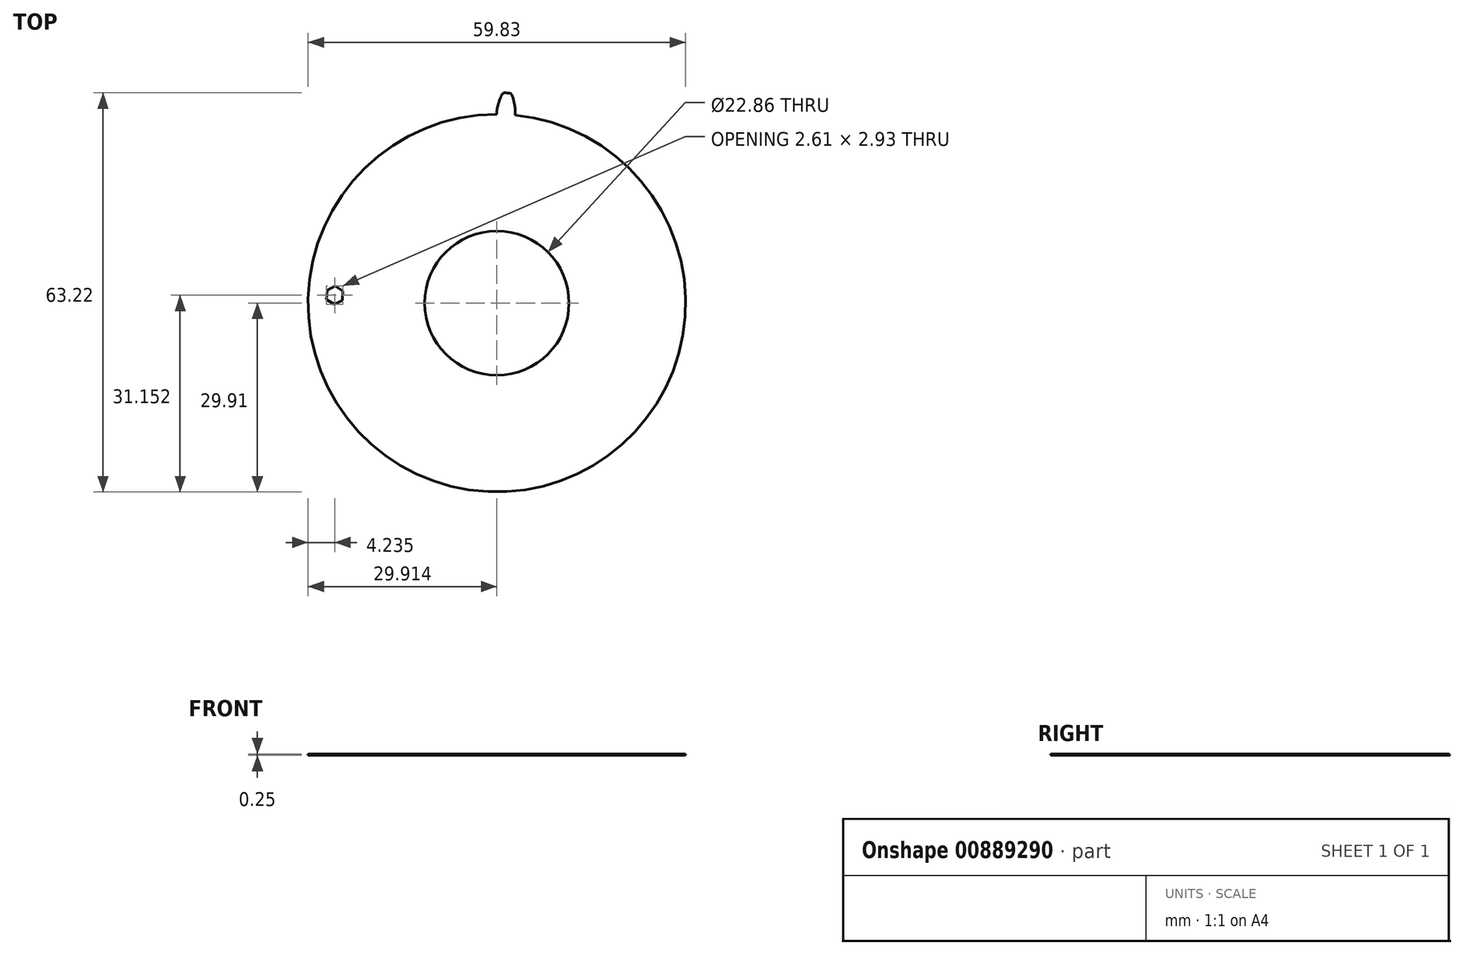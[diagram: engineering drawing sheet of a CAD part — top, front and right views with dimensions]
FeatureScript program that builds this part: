
annotation { "Feature Type Name" : "Feature", "Feature Type Description" : "" }
export const myFeature = defineFeature(function(context is Context, id is Id, definition is map)
    precondition{}
    {
        {
            assignVariable(context, id + "F0", {"name" : "N", "anyValue" : 16 * 2.5});
        }
        {
            assignVariable(context, id + "F1", {"name" : "Swid", "anyValue" : 0.25});
        }
        {
            var Q0;
            Q0=qCreatedBy(makeId("Top.planeOp"),FACE);
            var sketch = newSketch(context, id + "F2", { "sketchPlane" : qUnion([Q0])});
            skCircle(sketch, "E0", {"center": v(0, 0) * mm, "radius": 30.36 * mm, "construction": true});
            skCircle(sketch, "E1", {"center": v(0, 0) * mm, "radius": 31.75 * mm, "construction": true});
            skCircle(sketch, "E2", {"center": v(0, 0) * mm, "radius": 33.34 * mm});
            skLineSegment(sketch, "E3", {"start": v(0, 0) * mm, "end": v(0, 30.36) * mm, "construction": true});
            skLineSegment(sketch, "E4", {"start": v(0, 0) * mm, "end": v(1.99, 30.3) * mm, "construction": true});
            skLineSegment(sketch, "E5", {"start": v(0, 0) * mm, "end": v(3.96, 30.1) * mm, "construction": true});
            skLineSegment(sketch, "E6", {"start": v(0, 0) * mm, "end": v(5.92, 29.78) * mm, "construction": true});
            skLineSegment(sketch, "E7", {"start": v(0, 0) * mm, "end": v(7.86, 29.33) * mm, "construction": true});
            skCircle(sketch, "E8", {"center": v(0, 0) * mm, "radius": 29.91 * mm});
            skLineSegment(sketch, "E9", {"start": v(1.99, 30.3) * mm, "end": v(0, 30.43) * mm, "construction": true});
            skLineSegment(sketch, "E10", {"start": v(3.96, 30.1) * mm, "end": v(0.02, 30.62) * mm, "construction": true});
            skLineSegment(sketch, "E11", {"start": v(5.92, 29.78) * mm, "end": v(0.08, 30.94) * mm, "construction": true});
            skLineSegment(sketch, "E12", {"start": v(7.86, 29.33) * mm, "end": v(0.18, 31.39) * mm, "construction": true});
            skLineSegment(sketch, "E13", {"start": v(0, 0) * mm, "end": v(9.76, 28.75) * mm, "construction": true});
            skLineSegment(sketch, "E14", {"start": v(9.76, 28.75) * mm, "end": v(0.35, 31.95) * mm, "construction": true});
            skLineSegment(sketch, "E15", {"start": v(0, 0) * mm, "end": v(11.62, 28.05) * mm, "construction": true});
            skLineSegment(sketch, "E16", {"start": v(0, 0) * mm, "end": v(13.43, 27.23) * mm, "construction": true});
            skLineSegment(sketch, "E17", {"start": v(0, 0) * mm, "end": v(15.18, 26.3) * mm, "construction": true});
            skLineSegment(sketch, "E18", {"start": v(11.62, 28.05) * mm, "end": v(0.6, 32.61) * mm, "construction": true});
            skLineSegment(sketch, "E19", {"start": v(13.43, 27.23) * mm, "end": v(0.95, 33.38) * mm, "construction": true});
            skLineSegment(sketch, "E20", {"start": v(15.18, 26.3) * mm, "end": v(1.41, 34.24) * mm, "construction": true});
            skLineSegment(sketch, "E21", {"start": v(0, 0) * mm, "end": v(16.87, 25.25) * mm, "construction": true});
            skLineSegment(sketch, "E22", {"start": v(0, 0) * mm, "end": v(18.48, 24.09) * mm, "construction": true});
            skLineSegment(sketch, "E23", {"start": v(0, 0) * mm, "end": v(20.02, 22.83) * mm, "construction": true});
            skLineSegment(sketch, "E24", {"start": v(0, 0) * mm, "end": v(21.47, 21.47) * mm, "construction": true});
            skLineSegment(sketch, "E25", {"start": v(0, 0) * mm, "end": v(22.83, 20.02) * mm, "construction": true});
            skLineSegment(sketch, "E26", {"start": v(16.87, 25.25) * mm, "end": v(2, 35.18) * mm, "construction": true});
            skLineSegment(sketch, "E27", {"start": v(18.48, 24.09) * mm, "end": v(2.72, 36.19) * mm, "construction": true});
            skLineSegment(sketch, "E28", {"start": v(20.02, 22.83) * mm, "end": v(3.58, 37.24) * mm, "construction": true});
            skLineSegment(sketch, "E29", {"start": v(21.47, 21.47) * mm, "end": v(4.6, 38.33) * mm, "construction": true});
            skLineSegment(sketch, "E30", {"start": v(22.83, 20.02) * mm, "end": v(5.8, 39.44) * mm, "construction": true});
            skLineSegment(sketch, "E31", {"start": v(0, 0) * mm, "end": v(24.09, 18.48) * mm, "construction": true});
            skLineSegment(sketch, "E32", {"start": v(24.09, 18.48) * mm, "end": v(7.15, 40.56) * mm, "construction": true});
            skLineSegment(sketch, "E33", {"start": v(0, 0) * mm, "end": v(25.25, 16.87) * mm, "construction": true});
            skLineSegment(sketch, "E34", {"start": v(25.25, 16.87) * mm, "end": v(8.68, 41.65) * mm, "construction": true});
            skSolve(sketch);
        }
        {
            var Q0;
            Q0=qCreatedBy(makeId("Top.planeOp"),FACE);
            var sketch = newSketch(context, id + "F3", { "sketchPlane" : qUnion([Q0])});
            skLineSegment(sketch, "E35.0", {"start": v(24.09, 18.48) * mm, "end": v(7.15, 40.56) * mm, "construction": true});
            skLineSegment(sketch, "E35.1", {"start": v(22.83, 20.02) * mm, "end": v(5.8, 39.44) * mm, "construction": true});
            skLineSegment(sketch, "E35.2", {"start": v(21.47, 21.47) * mm, "end": v(4.6, 38.33) * mm, "construction": true});
            skLineSegment(sketch, "E35.3", {"start": v(20.02, 22.83) * mm, "end": v(3.58, 37.24) * mm, "construction": true});
            skLineSegment(sketch, "E35.4", {"start": v(18.48, 24.09) * mm, "end": v(2.72, 36.19) * mm, "construction": true});
            skLineSegment(sketch, "E35.5", {"start": v(16.87, 25.25) * mm, "end": v(2, 35.18) * mm, "construction": true});
            skLineSegment(sketch, "E35.6", {"start": v(15.18, 26.3) * mm, "end": v(1.41, 34.24) * mm, "construction": true});
            skLineSegment(sketch, "E35.7", {"start": v(13.43, 27.23) * mm, "end": v(0.95, 33.38) * mm, "construction": true});
            skLineSegment(sketch, "E35.8", {"start": v(11.62, 28.05) * mm, "end": v(0.6, 32.61) * mm, "construction": true});
            skLineSegment(sketch, "E35.9", {"start": v(9.76, 28.75) * mm, "end": v(0.35, 31.95) * mm, "construction": true});
            skLineSegment(sketch, "E35.10", {"start": v(7.86, 29.33) * mm, "end": v(0.18, 31.39) * mm, "construction": true});
            skLineSegment(sketch, "E35.11", {"start": v(5.92, 29.78) * mm, "end": v(0.08, 30.94) * mm, "construction": true});
            skLineSegment(sketch, "E35.12", {"start": v(3.96, 30.1) * mm, "end": v(0.02, 30.62) * mm, "construction": true});
            skLineSegment(sketch, "E35.13", {"start": v(1.99, 30.3) * mm, "end": v(0, 30.43) * mm, "construction": true});
            skCircle(sketch, "E35.14", {"center": v(0, 0) * mm, "radius": 30.36 * mm});
            skCircle(sketch, "E35.15", {"center": v(0, 0) * mm, "radius": 29.91 * mm});
            skCircle(sketch, "E35.16", {"center": v(0, 0) * mm, "radius": 31.75 * mm, "construction": true});
            skCircle(sketch, "E35.17", {"center": v(0, 0) * mm, "radius": 33.34 * mm});
            skLineSegment(sketch, "E36.0", {"start": v(25.25, 16.87) * mm, "end": v(8.68, 41.65) * mm, "construction": true});
            skLineSegment(sketch, "E37.0", {"start": v(0, 0) * mm, "end": v(0, 30.36) * mm, "construction": true});
            skFitSpline(sketch, "E38", {"points": [v(0, 30.36) * mm, v(0, 30.43) * mm, v(0.02, 30.62) * mm, v(0.08, 30.94) * mm, v(0.18, 31.39) * mm, v(0.35, 31.95) * mm, v(0.6, 32.61) * mm, v(0.95, 33.38) * mm, v(1.41, 34.24) * mm, v(2, 35.18) * mm, v(2.72, 36.19) * mm, v(3.58, 37.24) * mm, v(4.6, 38.33) * mm, v(5.8, 39.44) * mm, v(7.15, 40.56) * mm, v(8.68, 41.65) * mm, v(0, 0) * mm], "startDerivative": vector(0.68, 15.67) * mm, "endDerivative": vector(-81.92, -392.9) * mm});
            skLineSegment(sketch, "E39", {"start": v(0.29, 31.75) * mm, "end": v(0, 0) * mm, "construction": true});
            skLineSegment(sketch, "E40", {"start": v(0, 0) * mm, "end": v(1.6, 33.3) * mm, "construction": true});
            skFitSpline(sketch, "E41.MirrorCS", {"points": [v(2.93, 30.22) * mm, v(2.93, 30.29) * mm, v(2.93, 30.48) * mm, v(2.9, 30.8) * mm, v(2.85, 31.26) * mm, v(2.73, 31.83) * mm, v(2.54, 32.52) * mm, v(2.27, 33.32) * mm, v(1.9, 34.22) * mm, v(1.4, 35.21) * mm, v(0.78, 36.28) * mm, v(0.02, 37.41) * mm, v(-0.89, 38.6) * mm, v(-1.96, 39.82) * mm, v(-3.2, 41.06) * mm, v(-4.63, 42.3) * mm, v(0, 0) * mm], "startDerivative": vector(0.83, 15.67) * mm, "endDerivative": vector(43.65, -398.97) * mm});
            skLineSegment(sketch, "E42", {"start": v(2.93, 30.22) * mm, "end": v(2.88, 29.77) * mm});
            skLineSegment(sketch, "E43", {"start": v(0, 30.36) * mm, "end": v(0, 29.91) * mm});
            skSolve(sketch);
        }
        {
            var Q0;
            {var subQ3=sQuery(id+"F3.wireOp",EDGE,"E41.MirrorCS");var subQ6=sQuery(id+"F3.wireOp",EDGE,"E35.17");var subQ8=makeQuery(id+"F3.imprint","INTERSECT",VERTEX,{"disambiguationData":[OD(1.0)],"derivedFrom":[subQ6,subQ3]});Q0=makeQuery(id+"F3.imprint","IMPRINT",FACE,{"disambiguationData":[TD([[makeQuery(id+"F3.imprint","IMPRINT",EDGE,{"disambiguationData":[TD([[subQ8,-1.0]])],"derivedFrom":subQ6}),1.0]])]});}
            var Q1;
            {var subQ3=sQuery(id+"F3.wireOp",EDGE,"E41.MirrorCS");var subQ5=sQuery(id+"F3.wireOp",EDGE,"E35.15");var subQ6=makeQuery(id+"F3.imprint","INTERSECT",VERTEX,{"derivedFrom":[subQ5,subQ3]});Q1=makeQuery(id+"F3.imprint","IMPRINT",FACE,{"disambiguationData":[TD([[makeQuery(id+"F3.imprint","IMPRINT",EDGE,{"disambiguationData":[TD([[subQ6,-1.0]])],"derivedFrom":subQ5}),1.0]])]});}
            var Q2;
            {var subQ2=sQuery(id+"F3.wireOp",EDGE,"E42");Q2=makeQuery(id+"F3.imprint","IMPRINT",FACE,{"disambiguationData":[TD([[makeQuery(id+"F3.imprint","IMPRINT",EDGE,{"derivedFrom":subQ2}),-1.0]])]});}
            extrude(context, id + "F4", {"entities" : qUnion([Q0, Q1, Q2]), "depth" : (getVariable(context, 'Swid')) * mm, "offsetDistance" : 25.4 * mm});
        }
        {
            var Q0;
            Q0=qCreatedBy(makeId("Right.planeOp"),FACE);
            var sketch = newSketch(context, id + "F5", { "sketchPlane" : qUnion([Q0])});
            skLineSegment(sketch, "E44", {"start": v(0, 0) * mm, "end": v(0, 43.3) * mm, "construction": true});
            skSolve(sketch);
        }
        {
            var Q0;
            Q0=makeQuery(id+"F4.opExtrude","SWEPT_EDGE",EDGE,{"disambiguationData":[OSD([sQuery(id+"F3.wireOp",EDGE,"E35.17"),sQuery(id+"F3.wireOp",EDGE,"E41.MirrorCS")])]});
            var Q1;
            Q1=makeQuery(id+"F4.opExtrude","SWEPT_EDGE",EDGE,{"disambiguationData":[OSD([sQuery(id+"F3.wireOp",EDGE,"E35.17"),sQuery(id+"F3.wireOp",EDGE,"E38")])]});
            fillet(context, id + "F6", {"entities" : qUnion([Q0, Q1]), "radius" : 0.5 * mm, "tangentPropagation" : true, "allowEdgeOverflow" : false});
        }
        {
            var Q0;
            Q0=makeQuery(id+"F4.opExtrude","SWEPT_BODY",BODY,{"disambiguationData":[OSD([sQuery(id+"F3.wireOp",EDGE,"E35.15"),sQuery(id+"F3.wireOp",EDGE,"E35.17"),sQuery(id+"F3.wireOp",EDGE,"E38"),sQuery(id+"F3.wireOp",EDGE,"E41.MirrorCS"),sQuery(id+"F3.wireOp",EDGE,"9305e2c8-a00a-4cbc-a3b2-8fc88bc1717c"),sQuery(id+"F3.wireOp",EDGE,"f762f43d-eaf9-45ff-b6cd-062fd530227c")])]});
            var Q1;
            Q1=sQuery(id+"F5.wireOp",EDGE,"E44");
            circularPattern(context, id + "F7", {"operationType" : NewBodyOperationType.ADD, "entities" : qUnion([Q0]), "axis" : qUnion([Q1]), "angle" : (360 / getVariable(context, 'N')) * degree, "instanceCount" : getVariable(context, 'N'), "oppositeDirection" : true});
        }
        {
            var Q0;
            Q0=makeQuery(id+"F4.opExtrude","SWEPT_BODY",BODY,{"disambiguationData":[OSD([sQuery(id+"F3.wireOp",EDGE,"E35.15"),sQuery(id+"F3.wireOp",EDGE,"E35.17"),sQuery(id+"F3.wireOp",EDGE,"E38"),sQuery(id+"F3.wireOp",EDGE,"E41.MirrorCS"),sQuery(id+"F3.wireOp",EDGE,"E42"),sQuery(id+"F3.wireOp",EDGE,"E43")])]});
            transform(context, id + "F8", {"entities" : qUnion([Q0]), "transformType" : TransformType.TRANSLATION_3D, "dx" : 100.58 * mm, "dy" : 0 * mm, "dz" : 0 * mm, "makeCopy" : true});
        }
        {
            var Q0;
            {var subQ0=makeQuery(id+"F4.opExtrude","CAP_FACE",FACE,{"disambiguationData":[OSD([sQuery(id+"F3.wireOp",EDGE,"E35.15"),sQuery(id+"F3.wireOp",EDGE,"E35.17"),sQuery(id+"F3.wireOp",EDGE,"E38"),sQuery(id+"F3.wireOp",EDGE,"E41.MirrorCS"),sQuery(id+"F3.wireOp",EDGE,"E42"),sQuery(id+"F3.wireOp",EDGE,"E43")])],"isStart":false});Q0=makeQuery(id+"F7.boolean.opBoolean","MERGE",FACE,{"derivedFrom":[subQ0,makeQuery(id+"F7.opPattern","COPY",FACE,{"derivedFrom":subQ0,"instanceName":"1"}),makeQuery(id+"F7.opPattern","COPY",FACE,{"derivedFrom":subQ0,"instanceName":"2"}),makeQuery(id+"F7.opPattern","COPY",FACE,{"derivedFrom":subQ0,"instanceName":"3"}),makeQuery(id+"F7.opPattern","COPY",FACE,{"derivedFrom":subQ0,"instanceName":"4"}),makeQuery(id+"F7.opPattern","COPY",FACE,{"derivedFrom":subQ0,"instanceName":"5"}),makeQuery(id+"F7.opPattern","COPY",FACE,{"derivedFrom":subQ0,"instanceName":"6"}),makeQuery(id+"F7.opPattern","COPY",FACE,{"derivedFrom":subQ0,"instanceName":"7"}),makeQuery(id+"F7.opPattern","COPY",FACE,{"derivedFrom":subQ0,"instanceName":"8"}),makeQuery(id+"F7.opPattern","COPY",FACE,{"derivedFrom":subQ0,"instanceName":"9"}),makeQuery(id+"F7.opPattern","COPY",FACE,{"derivedFrom":subQ0,"instanceName":"10"}),makeQuery(id+"F7.opPattern","COPY",FACE,{"derivedFrom":subQ0,"instanceName":"11"}),makeQuery(id+"F7.opPattern","COPY",FACE,{"derivedFrom":subQ0,"instanceName":"12"}),makeQuery(id+"F7.opPattern","COPY",FACE,{"derivedFrom":subQ0,"instanceName":"13"}),makeQuery(id+"F7.opPattern","COPY",FACE,{"derivedFrom":subQ0,"instanceName":"14"}),makeQuery(id+"F7.opPattern","COPY",FACE,{"derivedFrom":subQ0,"instanceName":"15"}),makeQuery(id+"F7.opPattern","COPY",FACE,{"derivedFrom":subQ0,"instanceName":"16"}),makeQuery(id+"F7.opPattern","COPY",FACE,{"derivedFrom":subQ0,"instanceName":"17"}),makeQuery(id+"F7.opPattern","COPY",FACE,{"derivedFrom":subQ0,"instanceName":"18"}),makeQuery(id+"F7.opPattern","COPY",FACE,{"derivedFrom":subQ0,"instanceName":"19"}),makeQuery(id+"F7.opPattern","COPY",FACE,{"derivedFrom":subQ0,"instanceName":"20"}),makeQuery(id+"F7.opPattern","COPY",FACE,{"derivedFrom":subQ0,"instanceName":"21"}),makeQuery(id+"F7.opPattern","COPY",FACE,{"derivedFrom":subQ0,"instanceName":"22"}),makeQuery(id+"F7.opPattern","COPY",FACE,{"derivedFrom":subQ0,"instanceName":"23"}),makeQuery(id+"F7.opPattern","COPY",FACE,{"derivedFrom":subQ0,"instanceName":"24"}),makeQuery(id+"F7.opPattern","COPY",FACE,{"derivedFrom":subQ0,"instanceName":"25"}),makeQuery(id+"F7.opPattern","COPY",FACE,{"derivedFrom":subQ0,"instanceName":"26"}),makeQuery(id+"F7.opPattern","COPY",FACE,{"derivedFrom":subQ0,"instanceName":"27"}),makeQuery(id+"F7.opPattern","COPY",FACE,{"derivedFrom":subQ0,"instanceName":"28"}),makeQuery(id+"F7.opPattern","COPY",FACE,{"derivedFrom":subQ0,"instanceName":"29"}),makeQuery(id+"F7.opPattern","COPY",FACE,{"derivedFrom":subQ0,"instanceName":"30"}),makeQuery(id+"F7.opPattern","COPY",FACE,{"derivedFrom":subQ0,"instanceName":"31"}),makeQuery(id+"F7.opPattern","COPY",FACE,{"derivedFrom":subQ0,"instanceName":"32"}),makeQuery(id+"F7.opPattern","COPY",FACE,{"derivedFrom":subQ0,"instanceName":"33"}),makeQuery(id+"F7.opPattern","COPY",FACE,{"derivedFrom":subQ0,"instanceName":"34"}),makeQuery(id+"F7.opPattern","COPY",FACE,{"derivedFrom":subQ0,"instanceName":"35"}),makeQuery(id+"F7.opPattern","COPY",FACE,{"derivedFrom":subQ0,"instanceName":"36"}),makeQuery(id+"F7.opPattern","COPY",FACE,{"derivedFrom":subQ0,"instanceName":"37"}),makeQuery(id+"F7.opPattern","COPY",FACE,{"derivedFrom":subQ0,"instanceName":"38"}),makeQuery(id+"F7.opPattern","COPY",FACE,{"derivedFrom":subQ0,"instanceName":"39"})]});}
            var sketch = newSketch(context, id + "F9", { "sketchPlane" : qUnion([Q0])});
            skCircle(sketch, "E45", {"center": v(0, 0) * mm, "radius": 4.1 * mm});
            skLineSegment(sketch, "E46", {"start": v(29.9, 0.9) * mm, "end": v(0, 0) * mm, "construction": true});
            skLineSegment(sketch, "E47", {"start": v(2.62, -3.15) * mm, "end": v(2.43, 3.3) * mm});
            skSolve(sketch);
        }
        {
            var Q0;
            {var subQ0=sQuery(id+"F9.wireOp",EDGE,"E47");Q0=makeQuery(id+"F9.imprint","IMPRINT",FACE,{"disambiguationData":[TD([[makeQuery(id+"F9.imprint","IMPRINT",EDGE,{"derivedFrom":subQ0}),1.0]])]});}
            extrude(context, id + "F10", {"entities" : qUnion([Q0]), "operationType" : NewBodyOperationType.REMOVE, "endBound" : BoundingType.THROUGH_ALL, "oppositeDirection" : true, "depth" : 25.4 * mm, "offsetDistance" : 25.4 * mm});
        }
        {
            var Q0;
            {var subQ0=makeQuery(id+"F4.opExtrude","CAP_FACE",FACE,{"disambiguationData":[OSD([sQuery(id+"F3.wireOp",EDGE,"E35.15"),sQuery(id+"F3.wireOp",EDGE,"E35.17"),sQuery(id+"F3.wireOp",EDGE,"E38"),sQuery(id+"F3.wireOp",EDGE,"E41.MirrorCS"),sQuery(id+"F3.wireOp",EDGE,"E42"),sQuery(id+"F3.wireOp",EDGE,"E43")])],"isStart":false});Q0=makeQuery(id+"F7.boolean.opBoolean","MERGE",FACE,{"derivedFrom":[subQ0,makeQuery(id+"F7.opPattern","COPY",FACE,{"derivedFrom":subQ0,"instanceName":"1"}),makeQuery(id+"F7.opPattern","COPY",FACE,{"derivedFrom":subQ0,"instanceName":"2"}),makeQuery(id+"F7.opPattern","COPY",FACE,{"derivedFrom":subQ0,"instanceName":"3"}),makeQuery(id+"F7.opPattern","COPY",FACE,{"derivedFrom":subQ0,"instanceName":"4"}),makeQuery(id+"F7.opPattern","COPY",FACE,{"derivedFrom":subQ0,"instanceName":"5"}),makeQuery(id+"F7.opPattern","COPY",FACE,{"derivedFrom":subQ0,"instanceName":"6"}),makeQuery(id+"F7.opPattern","COPY",FACE,{"derivedFrom":subQ0,"instanceName":"7"}),makeQuery(id+"F7.opPattern","COPY",FACE,{"derivedFrom":subQ0,"instanceName":"8"}),makeQuery(id+"F7.opPattern","COPY",FACE,{"derivedFrom":subQ0,"instanceName":"9"}),makeQuery(id+"F7.opPattern","COPY",FACE,{"derivedFrom":subQ0,"instanceName":"10"}),makeQuery(id+"F7.opPattern","COPY",FACE,{"derivedFrom":subQ0,"instanceName":"11"}),makeQuery(id+"F7.opPattern","COPY",FACE,{"derivedFrom":subQ0,"instanceName":"12"}),makeQuery(id+"F7.opPattern","COPY",FACE,{"derivedFrom":subQ0,"instanceName":"13"}),makeQuery(id+"F7.opPattern","COPY",FACE,{"derivedFrom":subQ0,"instanceName":"14"}),makeQuery(id+"F7.opPattern","COPY",FACE,{"derivedFrom":subQ0,"instanceName":"15"}),makeQuery(id+"F7.opPattern","COPY",FACE,{"derivedFrom":subQ0,"instanceName":"16"}),makeQuery(id+"F7.opPattern","COPY",FACE,{"derivedFrom":subQ0,"instanceName":"17"}),makeQuery(id+"F7.opPattern","COPY",FACE,{"derivedFrom":subQ0,"instanceName":"18"}),makeQuery(id+"F7.opPattern","COPY",FACE,{"derivedFrom":subQ0,"instanceName":"19"}),makeQuery(id+"F7.opPattern","COPY",FACE,{"derivedFrom":subQ0,"instanceName":"20"}),makeQuery(id+"F7.opPattern","COPY",FACE,{"derivedFrom":subQ0,"instanceName":"21"}),makeQuery(id+"F7.opPattern","COPY",FACE,{"derivedFrom":subQ0,"instanceName":"22"}),makeQuery(id+"F7.opPattern","COPY",FACE,{"derivedFrom":subQ0,"instanceName":"23"}),makeQuery(id+"F7.opPattern","COPY",FACE,{"derivedFrom":subQ0,"instanceName":"24"}),makeQuery(id+"F7.opPattern","COPY",FACE,{"derivedFrom":subQ0,"instanceName":"25"}),makeQuery(id+"F7.opPattern","COPY",FACE,{"derivedFrom":subQ0,"instanceName":"26"}),makeQuery(id+"F7.opPattern","COPY",FACE,{"derivedFrom":subQ0,"instanceName":"27"}),makeQuery(id+"F7.opPattern","COPY",FACE,{"derivedFrom":subQ0,"instanceName":"28"}),makeQuery(id+"F7.opPattern","COPY",FACE,{"derivedFrom":subQ0,"instanceName":"29"}),makeQuery(id+"F7.opPattern","COPY",FACE,{"derivedFrom":subQ0,"instanceName":"30"}),makeQuery(id+"F7.opPattern","COPY",FACE,{"derivedFrom":subQ0,"instanceName":"31"}),makeQuery(id+"F7.opPattern","COPY",FACE,{"derivedFrom":subQ0,"instanceName":"32"}),makeQuery(id+"F7.opPattern","COPY",FACE,{"derivedFrom":subQ0,"instanceName":"33"}),makeQuery(id+"F7.opPattern","COPY",FACE,{"derivedFrom":subQ0,"instanceName":"34"}),makeQuery(id+"F7.opPattern","COPY",FACE,{"derivedFrom":subQ0,"instanceName":"35"}),makeQuery(id+"F7.opPattern","COPY",FACE,{"derivedFrom":subQ0,"instanceName":"36"}),makeQuery(id+"F7.opPattern","COPY",FACE,{"derivedFrom":subQ0,"instanceName":"37"}),makeQuery(id+"F7.opPattern","COPY",FACE,{"derivedFrom":subQ0,"instanceName":"38"}),makeQuery(id+"F7.opPattern","COPY",FACE,{"derivedFrom":subQ0,"instanceName":"39"})]});}
            var sketch = newSketch(context, id + "F11", { "sketchPlane" : qUnion([Q0])});
            skCircle(sketch, "E48", {"center": v(0, 0) * mm, "radius": 11.43 * mm});
            skCircle(sketch, "E49", {"center": v(26.09, 0.9) * mm, "radius": 1.27 * mm});
            skPoint(sketch, "E49.centerSnap0", {"position": v(29.9, 0.9) * mm});
            skSolve(sketch);
        }
        {
            var Q0;
            Q0=makeQuery(id+"F11.imprint","IMPRINT",FACE,{"disambiguationData":[TD([[makeQuery(id+"F11.imprint","IMPRINT",EDGE,{"derivedFrom":sQuery(id+"F11.wireOp",EDGE,"E48")}),1.0]])]});
            var Q1;
            Q1=makeQuery(id+"F11.imprint","IMPRINT",FACE,{"disambiguationData":[TD([[makeQuery(id+"F11.imprint","IMPRINT",EDGE,{"derivedFrom":sQuery(id+"F11.wireOp",EDGE,"ih8nmMkE-TSqh-M1XZ-P10M-uwXWHLw3eGEC")}),1.0]])]});
            var Q2;
            Q2=makeQuery(id+"F11.imprint","IMPRINT",FACE,{"disambiguationData":[TD([[makeQuery(id+"F11.imprint","IMPRINT",EDGE,{"derivedFrom":sQuery(id+"F11.wireOp",EDGE,"E49")}),1.0]])]});
            extrude(context, id + "F12", {"entities" : qUnion([Q0, Q1, Q2]), "operationType" : NewBodyOperationType.REMOVE, "oppositeDirection" : true, "depth" : 0.25 * mm, "offsetDistance" : 25.4 * mm});
        }
        {
            var Q0;
            {var subQ0=makeQuery(id+"F4.opExtrude","CAP_FACE",FACE,{"disambiguationData":[OSD([sQuery(id+"F3.wireOp",EDGE,"E35.15"),sQuery(id+"F3.wireOp",EDGE,"E35.17"),sQuery(id+"F3.wireOp",EDGE,"E38"),sQuery(id+"F3.wireOp",EDGE,"E41.MirrorCS"),sQuery(id+"F3.wireOp",EDGE,"E42"),sQuery(id+"F3.wireOp",EDGE,"E43")])],"isStart":false});Q0=makeQuery(id+"F8.opPattern","COPY",FACE,{"derivedFrom":makeQuery(id+"F7.boolean.opBoolean","MERGE",FACE,{"derivedFrom":[subQ0,makeQuery(id+"F7.opPattern","COPY",FACE,{"derivedFrom":subQ0,"instanceName":"1"}),makeQuery(id+"F7.opPattern","COPY",FACE,{"derivedFrom":subQ0,"instanceName":"2"}),makeQuery(id+"F7.opPattern","COPY",FACE,{"derivedFrom":subQ0,"instanceName":"3"}),makeQuery(id+"F7.opPattern","COPY",FACE,{"derivedFrom":subQ0,"instanceName":"4"}),makeQuery(id+"F7.opPattern","COPY",FACE,{"derivedFrom":subQ0,"instanceName":"5"}),makeQuery(id+"F7.opPattern","COPY",FACE,{"derivedFrom":subQ0,"instanceName":"6"}),makeQuery(id+"F7.opPattern","COPY",FACE,{"derivedFrom":subQ0,"instanceName":"7"}),makeQuery(id+"F7.opPattern","COPY",FACE,{"derivedFrom":subQ0,"instanceName":"8"}),makeQuery(id+"F7.opPattern","COPY",FACE,{"derivedFrom":subQ0,"instanceName":"9"}),makeQuery(id+"F7.opPattern","COPY",FACE,{"derivedFrom":subQ0,"instanceName":"10"}),makeQuery(id+"F7.opPattern","COPY",FACE,{"derivedFrom":subQ0,"instanceName":"11"}),makeQuery(id+"F7.opPattern","COPY",FACE,{"derivedFrom":subQ0,"instanceName":"12"}),makeQuery(id+"F7.opPattern","COPY",FACE,{"derivedFrom":subQ0,"instanceName":"13"}),makeQuery(id+"F7.opPattern","COPY",FACE,{"derivedFrom":subQ0,"instanceName":"14"}),makeQuery(id+"F7.opPattern","COPY",FACE,{"derivedFrom":subQ0,"instanceName":"15"}),makeQuery(id+"F7.opPattern","COPY",FACE,{"derivedFrom":subQ0,"instanceName":"16"}),makeQuery(id+"F7.opPattern","COPY",FACE,{"derivedFrom":subQ0,"instanceName":"17"}),makeQuery(id+"F7.opPattern","COPY",FACE,{"derivedFrom":subQ0,"instanceName":"18"}),makeQuery(id+"F7.opPattern","COPY",FACE,{"derivedFrom":subQ0,"instanceName":"19"}),makeQuery(id+"F7.opPattern","COPY",FACE,{"derivedFrom":subQ0,"instanceName":"20"}),makeQuery(id+"F7.opPattern","COPY",FACE,{"derivedFrom":subQ0,"instanceName":"21"}),makeQuery(id+"F7.opPattern","COPY",FACE,{"derivedFrom":subQ0,"instanceName":"22"}),makeQuery(id+"F7.opPattern","COPY",FACE,{"derivedFrom":subQ0,"instanceName":"23"}),makeQuery(id+"F7.opPattern","COPY",FACE,{"derivedFrom":subQ0,"instanceName":"24"}),makeQuery(id+"F7.opPattern","COPY",FACE,{"derivedFrom":subQ0,"instanceName":"25"}),makeQuery(id+"F7.opPattern","COPY",FACE,{"derivedFrom":subQ0,"instanceName":"26"}),makeQuery(id+"F7.opPattern","COPY",FACE,{"derivedFrom":subQ0,"instanceName":"27"}),makeQuery(id+"F7.opPattern","COPY",FACE,{"derivedFrom":subQ0,"instanceName":"28"}),makeQuery(id+"F7.opPattern","COPY",FACE,{"derivedFrom":subQ0,"instanceName":"29"}),makeQuery(id+"F7.opPattern","COPY",FACE,{"derivedFrom":subQ0,"instanceName":"30"}),makeQuery(id+"F7.opPattern","COPY",FACE,{"derivedFrom":subQ0,"instanceName":"31"}),makeQuery(id+"F7.opPattern","COPY",FACE,{"derivedFrom":subQ0,"instanceName":"32"}),makeQuery(id+"F7.opPattern","COPY",FACE,{"derivedFrom":subQ0,"instanceName":"33"}),makeQuery(id+"F7.opPattern","COPY",FACE,{"derivedFrom":subQ0,"instanceName":"34"}),makeQuery(id+"F7.opPattern","COPY",FACE,{"derivedFrom":subQ0,"instanceName":"35"}),makeQuery(id+"F7.opPattern","COPY",FACE,{"derivedFrom":subQ0,"instanceName":"36"}),makeQuery(id+"F7.opPattern","COPY",FACE,{"derivedFrom":subQ0,"instanceName":"37"}),makeQuery(id+"F7.opPattern","COPY",FACE,{"derivedFrom":subQ0,"instanceName":"38"}),makeQuery(id+"F7.opPattern","COPY",FACE,{"derivedFrom":subQ0,"instanceName":"39"})]}),"instanceName":"1"});}
            var sketch = newSketch(context, id + "F13", { "sketchPlane" : qUnion([Q0])});
            skCircle(sketch, "E50", {"center": v(100.58, 0) * mm, "radius": 4.1 * mm});
            skLineSegment(sketch, "E51", {"start": v(98.22, 3.35) * mm, "end": v(97.9, -3.1) * mm});
            skLineSegment(sketch, "E52", {"start": v(67.3, 1.6) * mm, "end": v(98.06, 0.12) * mm, "construction": true});
            skPoint(sketch, "E52.startSnap0", {"position": v(67.29, 1.6) * mm});
            skCircle(sketch, "E53.cCircle", {"center": v(74.9, 1.24) * mm, "radius": 1.27 * mm, "construction": true});
            skLineSegment(sketch, "E53.0", {"start": v(73.6, 0.57) * mm, "end": v(73.67, 2.04) * mm});
            skLineSegment(sketch, "E53.1", {"start": v(73.67, 2.04) * mm, "end": v(74.98, 2.7) * mm});
            skLineSegment(sketch, "E53.2", {"start": v(74.98, 2.7) * mm, "end": v(76.2, 1.91) * mm});
            skLineSegment(sketch, "E53.3", {"start": v(76.2, 1.91) * mm, "end": v(76.14, 0.45) * mm});
            skLineSegment(sketch, "E53.4", {"start": v(76.14, 0.45) * mm, "end": v(74.83, -0.22) * mm});
            skLineSegment(sketch, "E53.5", {"start": v(74.83, -0.22) * mm, "end": v(73.6, 0.57) * mm});
            skPoint(sketch, "E53.0.midPoint", {"position": v(73.64, 1.3) * mm});
            skSolve(sketch);
        }
        {
            var Q0;
            {var subQ0=sQuery(id+"F13.wireOp",EDGE,"E51");Q0=makeQuery(id+"F13.imprint","IMPRINT",FACE,{"disambiguationData":[TD([[makeQuery(id+"F13.imprint","IMPRINT",EDGE,{"derivedFrom":subQ0}),1.0]])]});}
            extrude(context, id + "F14", {"entities" : qUnion([Q0]), "operationType" : NewBodyOperationType.REMOVE, "oppositeDirection" : true, "depth" : 25.4 * mm, "offsetDistance" : 25.4 * mm});
        }
        {
            var Q0;
            {var subQ0=makeQuery(id+"F4.opExtrude","CAP_FACE",FACE,{"disambiguationData":[OSD([sQuery(id+"F3.wireOp",EDGE,"E35.15"),sQuery(id+"F3.wireOp",EDGE,"E35.17"),sQuery(id+"F3.wireOp",EDGE,"E38"),sQuery(id+"F3.wireOp",EDGE,"E41.MirrorCS"),sQuery(id+"F3.wireOp",EDGE,"E42"),sQuery(id+"F3.wireOp",EDGE,"E43")])],"isStart":false});Q0=makeQuery(id+"F8.opPattern","COPY",FACE,{"derivedFrom":makeQuery(id+"F7.boolean.opBoolean","MERGE",FACE,{"derivedFrom":[subQ0,makeQuery(id+"F7.opPattern","COPY",FACE,{"derivedFrom":subQ0,"instanceName":"1"}),makeQuery(id+"F7.opPattern","COPY",FACE,{"derivedFrom":subQ0,"instanceName":"2"}),makeQuery(id+"F7.opPattern","COPY",FACE,{"derivedFrom":subQ0,"instanceName":"3"}),makeQuery(id+"F7.opPattern","COPY",FACE,{"derivedFrom":subQ0,"instanceName":"4"}),makeQuery(id+"F7.opPattern","COPY",FACE,{"derivedFrom":subQ0,"instanceName":"5"}),makeQuery(id+"F7.opPattern","COPY",FACE,{"derivedFrom":subQ0,"instanceName":"6"}),makeQuery(id+"F7.opPattern","COPY",FACE,{"derivedFrom":subQ0,"instanceName":"7"}),makeQuery(id+"F7.opPattern","COPY",FACE,{"derivedFrom":subQ0,"instanceName":"8"}),makeQuery(id+"F7.opPattern","COPY",FACE,{"derivedFrom":subQ0,"instanceName":"9"}),makeQuery(id+"F7.opPattern","COPY",FACE,{"derivedFrom":subQ0,"instanceName":"10"}),makeQuery(id+"F7.opPattern","COPY",FACE,{"derivedFrom":subQ0,"instanceName":"11"}),makeQuery(id+"F7.opPattern","COPY",FACE,{"derivedFrom":subQ0,"instanceName":"12"}),makeQuery(id+"F7.opPattern","COPY",FACE,{"derivedFrom":subQ0,"instanceName":"13"}),makeQuery(id+"F7.opPattern","COPY",FACE,{"derivedFrom":subQ0,"instanceName":"14"}),makeQuery(id+"F7.opPattern","COPY",FACE,{"derivedFrom":subQ0,"instanceName":"15"}),makeQuery(id+"F7.opPattern","COPY",FACE,{"derivedFrom":subQ0,"instanceName":"16"}),makeQuery(id+"F7.opPattern","COPY",FACE,{"derivedFrom":subQ0,"instanceName":"17"}),makeQuery(id+"F7.opPattern","COPY",FACE,{"derivedFrom":subQ0,"instanceName":"18"}),makeQuery(id+"F7.opPattern","COPY",FACE,{"derivedFrom":subQ0,"instanceName":"19"}),makeQuery(id+"F7.opPattern","COPY",FACE,{"derivedFrom":subQ0,"instanceName":"20"}),makeQuery(id+"F7.opPattern","COPY",FACE,{"derivedFrom":subQ0,"instanceName":"21"}),makeQuery(id+"F7.opPattern","COPY",FACE,{"derivedFrom":subQ0,"instanceName":"22"}),makeQuery(id+"F7.opPattern","COPY",FACE,{"derivedFrom":subQ0,"instanceName":"23"}),makeQuery(id+"F7.opPattern","COPY",FACE,{"derivedFrom":subQ0,"instanceName":"24"}),makeQuery(id+"F7.opPattern","COPY",FACE,{"derivedFrom":subQ0,"instanceName":"25"}),makeQuery(id+"F7.opPattern","COPY",FACE,{"derivedFrom":subQ0,"instanceName":"26"}),makeQuery(id+"F7.opPattern","COPY",FACE,{"derivedFrom":subQ0,"instanceName":"27"}),makeQuery(id+"F7.opPattern","COPY",FACE,{"derivedFrom":subQ0,"instanceName":"28"}),makeQuery(id+"F7.opPattern","COPY",FACE,{"derivedFrom":subQ0,"instanceName":"29"}),makeQuery(id+"F7.opPattern","COPY",FACE,{"derivedFrom":subQ0,"instanceName":"30"}),makeQuery(id+"F7.opPattern","COPY",FACE,{"derivedFrom":subQ0,"instanceName":"31"}),makeQuery(id+"F7.opPattern","COPY",FACE,{"derivedFrom":subQ0,"instanceName":"32"}),makeQuery(id+"F7.opPattern","COPY",FACE,{"derivedFrom":subQ0,"instanceName":"33"}),makeQuery(id+"F7.opPattern","COPY",FACE,{"derivedFrom":subQ0,"instanceName":"34"}),makeQuery(id+"F7.opPattern","COPY",FACE,{"derivedFrom":subQ0,"instanceName":"35"}),makeQuery(id+"F7.opPattern","COPY",FACE,{"derivedFrom":subQ0,"instanceName":"36"}),makeQuery(id+"F7.opPattern","COPY",FACE,{"derivedFrom":subQ0,"instanceName":"37"}),makeQuery(id+"F7.opPattern","COPY",FACE,{"derivedFrom":subQ0,"instanceName":"38"}),makeQuery(id+"F7.opPattern","COPY",FACE,{"derivedFrom":subQ0,"instanceName":"39"})]}),"instanceName":"1"});}
            var sketch = newSketch(context, id + "F15", { "sketchPlane" : qUnion([Q0])});
            skCircle(sketch, "E54", {"center": v(100.58, 0) * mm, "radius": 11.43 * mm});
            skLineSegment(sketch, "E55.0.0", {"start": v(73.6, 0.57) * mm, "end": v(74.83, -0.22) * mm});
            skLineSegment(sketch, "E55.0.1", {"start": v(74.83, -0.22) * mm, "end": v(76.14, 0.45) * mm});
            skLineSegment(sketch, "E55.0.2", {"start": v(76.14, 0.45) * mm, "end": v(76.2, 1.91) * mm});
            skLineSegment(sketch, "E55.0.3", {"start": v(76.2, 1.91) * mm, "end": v(74.98, 2.7) * mm});
            skLineSegment(sketch, "E55.0.4", {"start": v(74.98, 2.7) * mm, "end": v(73.67, 2.04) * mm});
            skLineSegment(sketch, "E55.0.5", {"start": v(73.67, 2.04) * mm, "end": v(73.6, 0.57) * mm});
            skSolve(sketch);
        }
        {
            var Q0;
            Q0 = qSketchRegion(id + "F15", true);
            extrude(context, id + "F16", {"entities" : qUnion([Q0]), "operationType" : NewBodyOperationType.REMOVE, "oppositeDirection" : true, "depth" : 0.25 * mm, "offsetDistance" : 25.4 * mm});
        }
        {
            var Q0;
            {var subQ0=makeQuery(id+"F4.opExtrude","CAP_FACE",FACE,{"disambiguationData":[OSD([sQuery(id+"F3.wireOp",EDGE,"E35.15"),sQuery(id+"F3.wireOp",EDGE,"E35.17"),sQuery(id+"F3.wireOp",EDGE,"E38"),sQuery(id+"F3.wireOp",EDGE,"E41.MirrorCS"),sQuery(id+"F3.wireOp",EDGE,"E42"),sQuery(id+"F3.wireOp",EDGE,"E43")])],"isStart":true});Q0=makeQuery(id+"F8.opPattern","COPY",FACE,{"derivedFrom":makeQuery(id+"F7.boolean.opBoolean","MERGE",FACE,{"derivedFrom":[subQ0,makeQuery(id+"F7.opPattern","COPY",FACE,{"derivedFrom":subQ0,"instanceName":"1"}),makeQuery(id+"F7.opPattern","COPY",FACE,{"derivedFrom":subQ0,"instanceName":"2"}),makeQuery(id+"F7.opPattern","COPY",FACE,{"derivedFrom":subQ0,"instanceName":"3"}),makeQuery(id+"F7.opPattern","COPY",FACE,{"derivedFrom":subQ0,"instanceName":"4"}),makeQuery(id+"F7.opPattern","COPY",FACE,{"derivedFrom":subQ0,"instanceName":"5"}),makeQuery(id+"F7.opPattern","COPY",FACE,{"derivedFrom":subQ0,"instanceName":"6"}),makeQuery(id+"F7.opPattern","COPY",FACE,{"derivedFrom":subQ0,"instanceName":"7"}),makeQuery(id+"F7.opPattern","COPY",FACE,{"derivedFrom":subQ0,"instanceName":"8"}),makeQuery(id+"F7.opPattern","COPY",FACE,{"derivedFrom":subQ0,"instanceName":"9"}),makeQuery(id+"F7.opPattern","COPY",FACE,{"derivedFrom":subQ0,"instanceName":"10"}),makeQuery(id+"F7.opPattern","COPY",FACE,{"derivedFrom":subQ0,"instanceName":"11"}),makeQuery(id+"F7.opPattern","COPY",FACE,{"derivedFrom":subQ0,"instanceName":"12"}),makeQuery(id+"F7.opPattern","COPY",FACE,{"derivedFrom":subQ0,"instanceName":"13"}),makeQuery(id+"F7.opPattern","COPY",FACE,{"derivedFrom":subQ0,"instanceName":"14"}),makeQuery(id+"F7.opPattern","COPY",FACE,{"derivedFrom":subQ0,"instanceName":"15"}),makeQuery(id+"F7.opPattern","COPY",FACE,{"derivedFrom":subQ0,"instanceName":"16"}),makeQuery(id+"F7.opPattern","COPY",FACE,{"derivedFrom":subQ0,"instanceName":"17"}),makeQuery(id+"F7.opPattern","COPY",FACE,{"derivedFrom":subQ0,"instanceName":"18"}),makeQuery(id+"F7.opPattern","COPY",FACE,{"derivedFrom":subQ0,"instanceName":"19"}),makeQuery(id+"F7.opPattern","COPY",FACE,{"derivedFrom":subQ0,"instanceName":"20"}),makeQuery(id+"F7.opPattern","COPY",FACE,{"derivedFrom":subQ0,"instanceName":"21"}),makeQuery(id+"F7.opPattern","COPY",FACE,{"derivedFrom":subQ0,"instanceName":"22"}),makeQuery(id+"F7.opPattern","COPY",FACE,{"derivedFrom":subQ0,"instanceName":"23"}),makeQuery(id+"F7.opPattern","COPY",FACE,{"derivedFrom":subQ0,"instanceName":"24"}),makeQuery(id+"F7.opPattern","COPY",FACE,{"derivedFrom":subQ0,"instanceName":"25"}),makeQuery(id+"F7.opPattern","COPY",FACE,{"derivedFrom":subQ0,"instanceName":"26"}),makeQuery(id+"F7.opPattern","COPY",FACE,{"derivedFrom":subQ0,"instanceName":"27"}),makeQuery(id+"F7.opPattern","COPY",FACE,{"derivedFrom":subQ0,"instanceName":"28"}),makeQuery(id+"F7.opPattern","COPY",FACE,{"derivedFrom":subQ0,"instanceName":"29"}),makeQuery(id+"F7.opPattern","COPY",FACE,{"derivedFrom":subQ0,"instanceName":"30"}),makeQuery(id+"F7.opPattern","COPY",FACE,{"derivedFrom":subQ0,"instanceName":"31"}),makeQuery(id+"F7.opPattern","COPY",FACE,{"derivedFrom":subQ0,"instanceName":"32"}),makeQuery(id+"F7.opPattern","COPY",FACE,{"derivedFrom":subQ0,"instanceName":"33"}),makeQuery(id+"F7.opPattern","COPY",FACE,{"derivedFrom":subQ0,"instanceName":"34"}),makeQuery(id+"F7.opPattern","COPY",FACE,{"derivedFrom":subQ0,"instanceName":"35"}),makeQuery(id+"F7.opPattern","COPY",FACE,{"derivedFrom":subQ0,"instanceName":"36"}),makeQuery(id+"F7.opPattern","COPY",FACE,{"derivedFrom":subQ0,"instanceName":"37"}),makeQuery(id+"F7.opPattern","COPY",FACE,{"derivedFrom":subQ0,"instanceName":"38"}),makeQuery(id+"F7.opPattern","COPY",FACE,{"derivedFrom":subQ0,"instanceName":"39"})]}),"instanceName":"1"});}
            var sketch = newSketch(context, id + "F17", { "sketchPlane" : qUnion([Q0])});
            skLineSegment(sketch, "E56.0.0", {"start": v(74.98, -2.7) * mm, "end": v(73.67, -2.04) * mm});
            skLineSegment(sketch, "E56.0.1", {"start": v(73.67, -2.04) * mm, "end": v(73.6, -0.57) * mm});
            skLineSegment(sketch, "E56.0.2", {"start": v(73.6, -0.57) * mm, "end": v(74.83, 0.22) * mm});
            skLineSegment(sketch, "E56.0.3", {"start": v(74.83, 0.22) * mm, "end": v(76.14, -0.45) * mm});
            skLineSegment(sketch, "E56.0.4", {"start": v(76.14, -0.45) * mm, "end": v(76.2, -1.91) * mm});
            skLineSegment(sketch, "E56.0.5", {"start": v(76.2, -1.91) * mm, "end": v(74.98, -2.7) * mm});
            skSolve(sketch);
        }
        {
            var Q0;
            Q0=makeQuery(id+"F17.imprint","IMPRINT",FACE,{"disambiguationData":[TD([[makeQuery(id+"F17.imprint","IMPRINT",EDGE,{"derivedFrom":sQuery(id+"F17.wireOp",EDGE,"E56.0.0")}),-1.0]])]});
            extrude(context, id + "F18", {"entities" : qUnion([Q0]), "operationType" : NewBodyOperationType.REMOVE, "oppositeDirection" : true, "depth" : 0.25 * mm, "offsetDistance" : 25.4 * mm});
        }
        {
            var Q0;
            {var subQ0=makeQuery(id+"F4.opExtrude","CAP_FACE",FACE,{"disambiguationData":[OSD([sQuery(id+"F3.wireOp",EDGE,"E35.15"),sQuery(id+"F3.wireOp",EDGE,"E35.17"),sQuery(id+"F3.wireOp",EDGE,"E38"),sQuery(id+"F3.wireOp",EDGE,"E41.MirrorCS"),sQuery(id+"F3.wireOp",EDGE,"E42"),sQuery(id+"F3.wireOp",EDGE,"E43")])],"isStart":true});Q0=makeQuery(id+"F7.boolean.opBoolean","MERGE",FACE,{"derivedFrom":[subQ0,makeQuery(id+"F7.opPattern","COPY",FACE,{"derivedFrom":subQ0,"instanceName":"1"}),makeQuery(id+"F7.opPattern","COPY",FACE,{"derivedFrom":subQ0,"instanceName":"2"}),makeQuery(id+"F7.opPattern","COPY",FACE,{"derivedFrom":subQ0,"instanceName":"3"}),makeQuery(id+"F7.opPattern","COPY",FACE,{"derivedFrom":subQ0,"instanceName":"4"}),makeQuery(id+"F7.opPattern","COPY",FACE,{"derivedFrom":subQ0,"instanceName":"5"}),makeQuery(id+"F7.opPattern","COPY",FACE,{"derivedFrom":subQ0,"instanceName":"6"}),makeQuery(id+"F7.opPattern","COPY",FACE,{"derivedFrom":subQ0,"instanceName":"7"}),makeQuery(id+"F7.opPattern","COPY",FACE,{"derivedFrom":subQ0,"instanceName":"8"}),makeQuery(id+"F7.opPattern","COPY",FACE,{"derivedFrom":subQ0,"instanceName":"9"}),makeQuery(id+"F7.opPattern","COPY",FACE,{"derivedFrom":subQ0,"instanceName":"10"}),makeQuery(id+"F7.opPattern","COPY",FACE,{"derivedFrom":subQ0,"instanceName":"11"}),makeQuery(id+"F7.opPattern","COPY",FACE,{"derivedFrom":subQ0,"instanceName":"12"}),makeQuery(id+"F7.opPattern","COPY",FACE,{"derivedFrom":subQ0,"instanceName":"13"}),makeQuery(id+"F7.opPattern","COPY",FACE,{"derivedFrom":subQ0,"instanceName":"14"}),makeQuery(id+"F7.opPattern","COPY",FACE,{"derivedFrom":subQ0,"instanceName":"15"}),makeQuery(id+"F7.opPattern","COPY",FACE,{"derivedFrom":subQ0,"instanceName":"16"}),makeQuery(id+"F7.opPattern","COPY",FACE,{"derivedFrom":subQ0,"instanceName":"17"}),makeQuery(id+"F7.opPattern","COPY",FACE,{"derivedFrom":subQ0,"instanceName":"18"}),makeQuery(id+"F7.opPattern","COPY",FACE,{"derivedFrom":subQ0,"instanceName":"19"}),makeQuery(id+"F7.opPattern","COPY",FACE,{"derivedFrom":subQ0,"instanceName":"20"}),makeQuery(id+"F7.opPattern","COPY",FACE,{"derivedFrom":subQ0,"instanceName":"21"}),makeQuery(id+"F7.opPattern","COPY",FACE,{"derivedFrom":subQ0,"instanceName":"22"}),makeQuery(id+"F7.opPattern","COPY",FACE,{"derivedFrom":subQ0,"instanceName":"23"}),makeQuery(id+"F7.opPattern","COPY",FACE,{"derivedFrom":subQ0,"instanceName":"24"}),makeQuery(id+"F7.opPattern","COPY",FACE,{"derivedFrom":subQ0,"instanceName":"25"}),makeQuery(id+"F7.opPattern","COPY",FACE,{"derivedFrom":subQ0,"instanceName":"26"}),makeQuery(id+"F7.opPattern","COPY",FACE,{"derivedFrom":subQ0,"instanceName":"27"}),makeQuery(id+"F7.opPattern","COPY",FACE,{"derivedFrom":subQ0,"instanceName":"28"}),makeQuery(id+"F7.opPattern","COPY",FACE,{"derivedFrom":subQ0,"instanceName":"29"}),makeQuery(id+"F7.opPattern","COPY",FACE,{"derivedFrom":subQ0,"instanceName":"30"}),makeQuery(id+"F7.opPattern","COPY",FACE,{"derivedFrom":subQ0,"instanceName":"31"}),makeQuery(id+"F7.opPattern","COPY",FACE,{"derivedFrom":subQ0,"instanceName":"32"}),makeQuery(id+"F7.opPattern","COPY",FACE,{"derivedFrom":subQ0,"instanceName":"33"}),makeQuery(id+"F7.opPattern","COPY",FACE,{"derivedFrom":subQ0,"instanceName":"34"}),makeQuery(id+"F7.opPattern","COPY",FACE,{"derivedFrom":subQ0,"instanceName":"35"}),makeQuery(id+"F7.opPattern","COPY",FACE,{"derivedFrom":subQ0,"instanceName":"36"}),makeQuery(id+"F7.opPattern","COPY",FACE,{"derivedFrom":subQ0,"instanceName":"37"}),makeQuery(id+"F7.opPattern","COPY",FACE,{"derivedFrom":subQ0,"instanceName":"38"}),makeQuery(id+"F7.opPattern","COPY",FACE,{"derivedFrom":subQ0,"instanceName":"39"})]});}
            var sketch = newSketch(context, id + "F19", { "sketchPlane" : qUnion([Q0])});
            skCircle(sketch, "E57.0.0", {"center": v(26.09, -0.9) * mm, "radius": 1.27 * mm});
            skSolve(sketch);
        }
        {
            var Q0;
            Q0=makeQuery(id+"F19.imprint","IMPRINT",FACE,{"disambiguationData":[TD([[makeQuery(id+"F19.imprint","IMPRINT",EDGE,{"derivedFrom":sQuery(id+"F19.wireOp",EDGE,"E57.0.0")}),1.0]])]});
            extrude(context, id + "F20", {"entities" : qUnion([Q0]), "operationType" : NewBodyOperationType.REMOVE, "oppositeDirection" : true, "depth" : 0.25 * mm, "offsetDistance" : 25.4 * mm});
        }
    });
